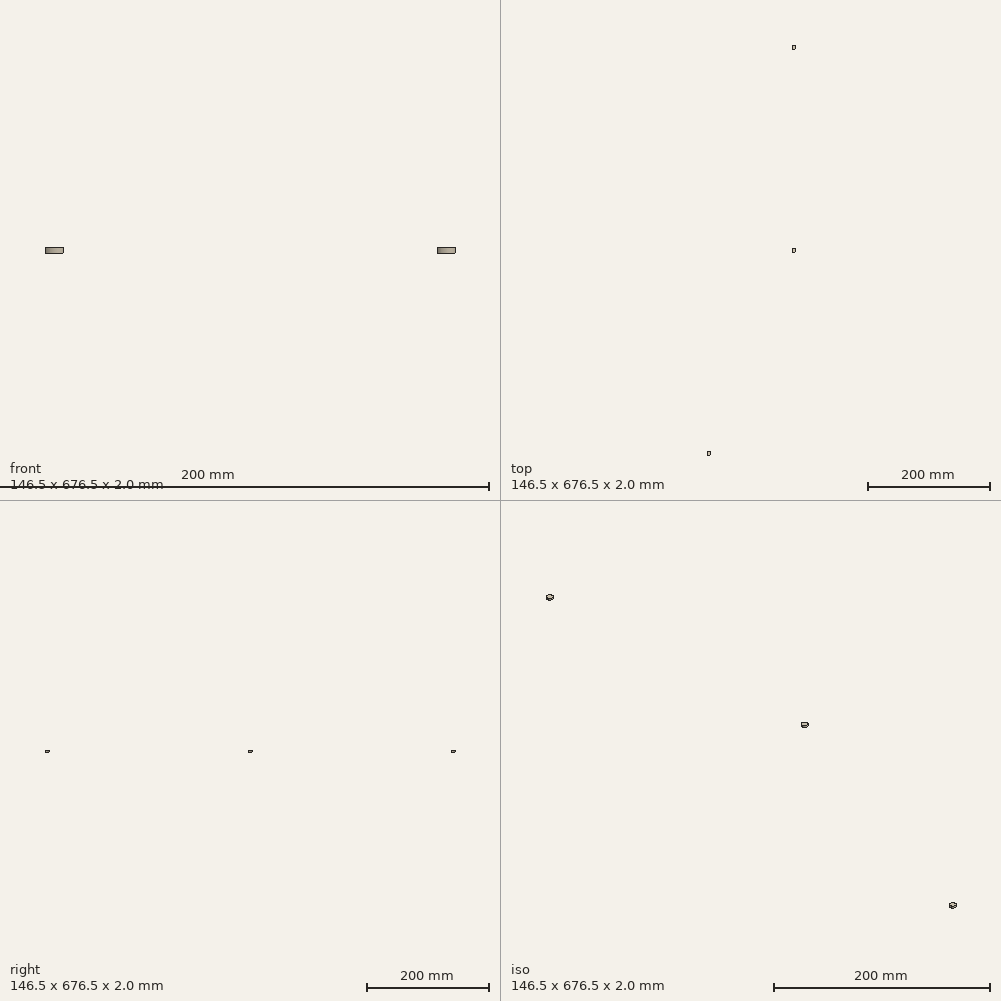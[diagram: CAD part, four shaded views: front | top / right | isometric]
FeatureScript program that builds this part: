
annotation { "Feature Type Name" : "Feature", "Feature Type Description" : "" }
export const myFeature = defineFeature(function(context is Context, id is Id, definition is map)
    precondition{}
    {
        {
            var Q0;
            Q0=qCreatedBy(makeId("Top.planeOp"),FACE);
            var sketch = newSketch(context, id + "F0", { "sketchPlane" : qUnion([Q0])});
            skLineSegment(sketch, "E0.bottom", {"start": v(80, -345) * mm, "end": v(-80, -345) * mm});
            skLineSegment(sketch, "E0.top", {"start": v(80, 345) * mm, "end": v(-80, 345) * mm});
            skLineSegment(sketch, "E0.left", {"start": v(80, -345) * mm, "end": v(80, 345) * mm});
            skLineSegment(sketch, "E0.right", {"start": v(-80, -345) * mm, "end": v(-80, 345) * mm});
            skPoint(sketch, "E0.middle", {"position": v(0, 0) * mm});
            skSolve(sketch);
        }
        {
            var Q0;
            Q0=makeQuery(id+"F0.imprint","IMPRINT",FACE,{"disambiguationData":[TD([[makeQuery(id+"F0.imprint","IMPRINT",EDGE,{"derivedFrom":sQuery(id+"F0.wireOp",EDGE,"E0.bottom")}),-1.0]])]});
            extrude(context, id + "F1", {"entities" : qUnion([Q0]), "depth" : 2 * mm});
        }
        {
            var Q0;
            Q0=makeQuery(id+"F1.opExtrude","CAP_FACE",FACE,{"disambiguationData":[OSD([sQuery(id+"F0.wireOp",EDGE,"E0.bottom"),sQuery(id+"F0.wireOp",EDGE,"E0.top"),sQuery(id+"F0.wireOp",EDGE,"E0.left"),sQuery(id+"F0.wireOp",EDGE,"E0.right")])],"isStart":false});
            var sketch = newSketch(context, id + "F2", { "sketchPlane" : qUnion([Q0])});
            skCircle(sketch, "E1", {"center": v(-70, 335) * mm, "radius": 3.25 * mm});
            skCircle(sketch, "E2.MirrorC", {"center": v(70, 335) * mm, "radius": 3.25 * mm});
            skCircle(sketch, "E3.MirrorC", {"center": v(-70, -335) * mm, "radius": 3.25 * mm});
            skCircle(sketch, "E4.MirrorC", {"center": v(70, -335) * mm, "radius": 3.25 * mm});
            skCircle(sketch, "E5", {"center": v(-70, 0) * mm, "radius": 3.25 * mm});
            skCircle(sketch, "E6.MirrorC", {"center": v(70, 0) * mm, "radius": 3.25 * mm});
            skSolve(sketch);
        }
        {
            var Q0;
            Q0=makeQuery(id+"F2.imprint","IMPRINT",FACE,{"disambiguationData":[TD([[makeQuery(id+"F2.imprint","IMPRINT",EDGE,{"derivedFrom":sQuery(id+"F2.wireOp",EDGE,"E1")}),1.0]])]});
            var Q1;
            Q1=makeQuery(id+"F2.imprint","IMPRINT",FACE,{"disambiguationData":[TD([[makeQuery(id+"F2.imprint","IMPRINT",EDGE,{"derivedFrom":sQuery(id+"F2.wireOp",EDGE,"E2.MirrorC")}),-1.0]])]});
            var Q2;
            Q2=makeQuery(id+"F2.imprint","IMPRINT",FACE,{"disambiguationData":[TD([[makeQuery(id+"F2.imprint","IMPRINT",EDGE,{"derivedFrom":sQuery(id+"F2.wireOp",EDGE,"E3.MirrorC")}),-1.0]])]});
            var Q3;
            Q3=makeQuery(id+"F2.imprint","IMPRINT",FACE,{"disambiguationData":[TD([[makeQuery(id+"F2.imprint","IMPRINT",EDGE,{"derivedFrom":sQuery(id+"F2.wireOp",EDGE,"E4.MirrorC")}),1.0]])]});
            var Q4;
            Q4=makeQuery(id+"F2.imprint","IMPRINT",FACE,{"disambiguationData":[TD([[makeQuery(id+"F2.imprint","IMPRINT",EDGE,{"derivedFrom":sQuery(id+"F2.wireOp",EDGE,"E5")}),1.0]])]});
            var Q5;
            Q5=makeQuery(id+"F2.imprint","IMPRINT",FACE,{"disambiguationData":[TD([[makeQuery(id+"F2.imprint","IMPRINT",EDGE,{"derivedFrom":sQuery(id+"F2.wireOp",EDGE,"E6.MirrorC")}),-1.0]])]});
            extrude(context, id + "F3", {"entities" : qUnion([Q0, Q1, Q2, Q3, Q4, Q5]), "operationType" : NewBodyOperationType.REMOVE, "oppositeDirection" : true, "depth" : 25 * mm});
        }
    });
